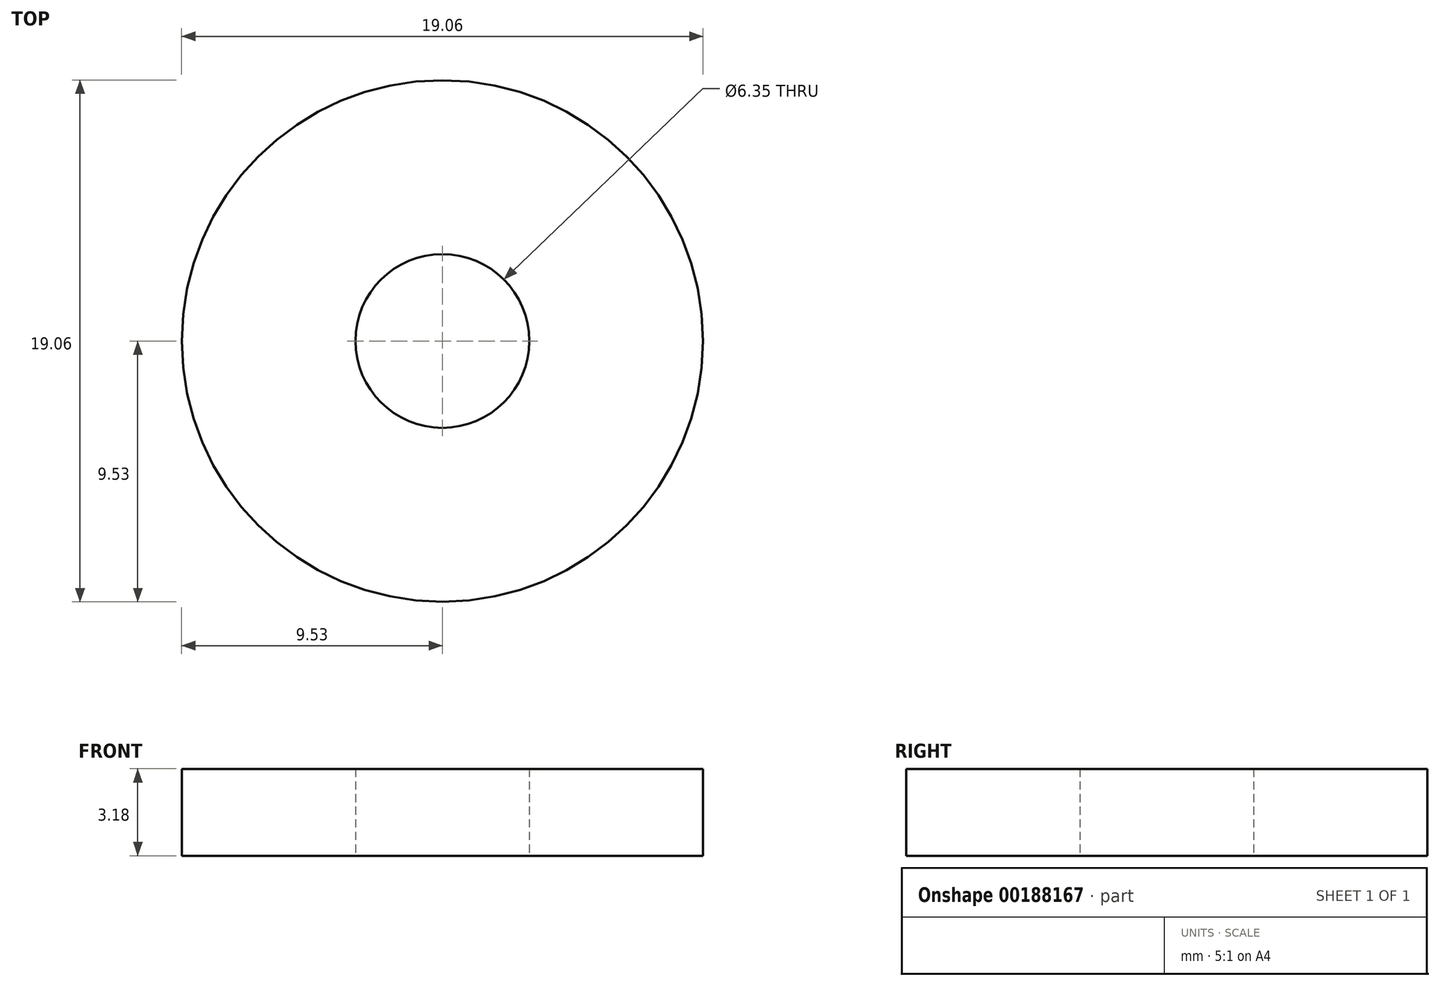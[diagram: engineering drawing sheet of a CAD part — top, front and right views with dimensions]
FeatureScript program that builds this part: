
annotation { "Feature Type Name" : "Feature", "Feature Type Description" : "" }
export const myFeature = defineFeature(function(context is Context, id is Id, definition is map)
    precondition{}
    {
        {
            var Q0;
            Q0=qCreatedBy(makeId("Top.planeOp"),FACE);
            var sketch = newSketch(context, id + "F0", { "sketchPlane" : qUnion([Q0])});
            skCircle(sketch, "E0", {"center": v(0, 0) * mm, "radius": 9.53 * mm});
            skCircle(sketch, "E1", {"center": v(0, 0) * mm, "radius": 3.17 * mm});
            skSolve(sketch);
        }
        {
            var Q0;
            Q0=makeQuery(id+"F0.imprint","IMPRINT",FACE,{"disambiguationData":[TD([[makeQuery(id+"F0.imprint","IMPRINT",EDGE,{"derivedFrom":sQuery(id+"F0.wireOp",EDGE,"E0")}),1.0]])]});
            extrude(context, id + "F1", {"entities" : qUnion([Q0]), "depth" : 3.17 * mm});
        }
    });
